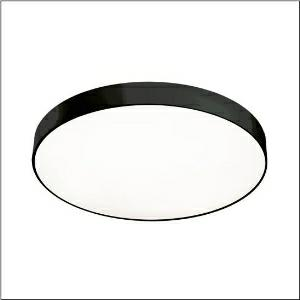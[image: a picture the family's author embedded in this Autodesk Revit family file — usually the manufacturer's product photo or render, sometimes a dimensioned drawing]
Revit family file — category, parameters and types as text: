
# Revit family: round_21_l_51mr38fd0421b
name_source: partatom
category: Lighting Fixtures
units: mm (PartAtom-declared; Revit-internal decimal feet)

## family parameters
Cut with Voids When Loaded = No
Host = Face
Light Source = No
Part Type = Normal
Room Calculation Point = No
Round Connector Dimension = Use Diameter
Shared = No

## types (1)
- Round 21 L (1 x LED, 14150 lm, 97 W, 4000K)
    Apparent Load = 97 VA
    CIE Flux Codes = 49 80 96 100 100
    Color Rendering = 80
    Color Temperature = 4000K
    Default Elevation = 1800 mm
    Description = Round 21 L, wall and ceiling luminaire, primary optical cover: cover, of PMMA, opal, light emission: direct distribution, primary light characteristic: symmetric, installation type: suspended mounting, surface-mounted, LED, rated luminous flux: 13.080lm, luminous efficacy: 146lm/W, light colour: 840, colour temperature: 4000K, control gear: DALI 2, with terminal, 5-pole, mains connection: 230V, AC, 50/60Hz, rated input power: 97W, housing, of aluminium, coated, black, diameter: 850mm, height: 62mm, protection rating (complete): IP40, insulation class (complete): insulation class I (protective earthing), certification: CE, impact resistance: IK04, permissible operating ambient temperature: -10..+35°C, packaging unit: 1 piece
    Height = 87 mm
    Lamp = 1 x LED
    Lamp Light Flux = 14150 lm
    Lamp Power = 97 W
    Lamp count = 1
    Length = 850 mm
    Luminous efficacy = 146 lm/W
    Manufacturer = Siteco
    ModVariant = No
    Model = 51MR38FD0421B
    Mounting Place = Ceiling
    Mounting Type = Surface mounted
    Number of Poles = 1
    OnlyDefault = Yes
    Power Factor = 1
    Product Name = Round 21 L
    Product group = wall and ceiling luminaire | ceiling mounted
    ProductGroupID = 305
    Protection Class = Protection class I
    Protection Degree = IP 40
    RLX_Detail_Level = 1
    RLX_Emergency_Light_Flux = 0 lm
    RLX_Emergency_Type = 0
    RLX_Emergency_Type_DB = No
    RlxData = <blob elided: 23937 chars, md5=beb2a0b5>
    Socket = socket
    Standby Power = 0 W
    System Light Flux = 14150 lm
    System Power = 97 W
    Type Comments = Product without accessories
    Type Image = l_1258328.jpg
    URL = http://relux.com
    VarID = ---
    Voltage = 0 V
    Weight = 0.00 kg
    Width = 0 mm  [stored 0 ft]

note: [stored X ft] marks values corroborated as IEEE doubles in the binary element streams (Revit-internal decimal feet)

## geometry (parser evidence)
native form markers: Blend x4, Sweep x10
no freeform markers — native parametric forms only
